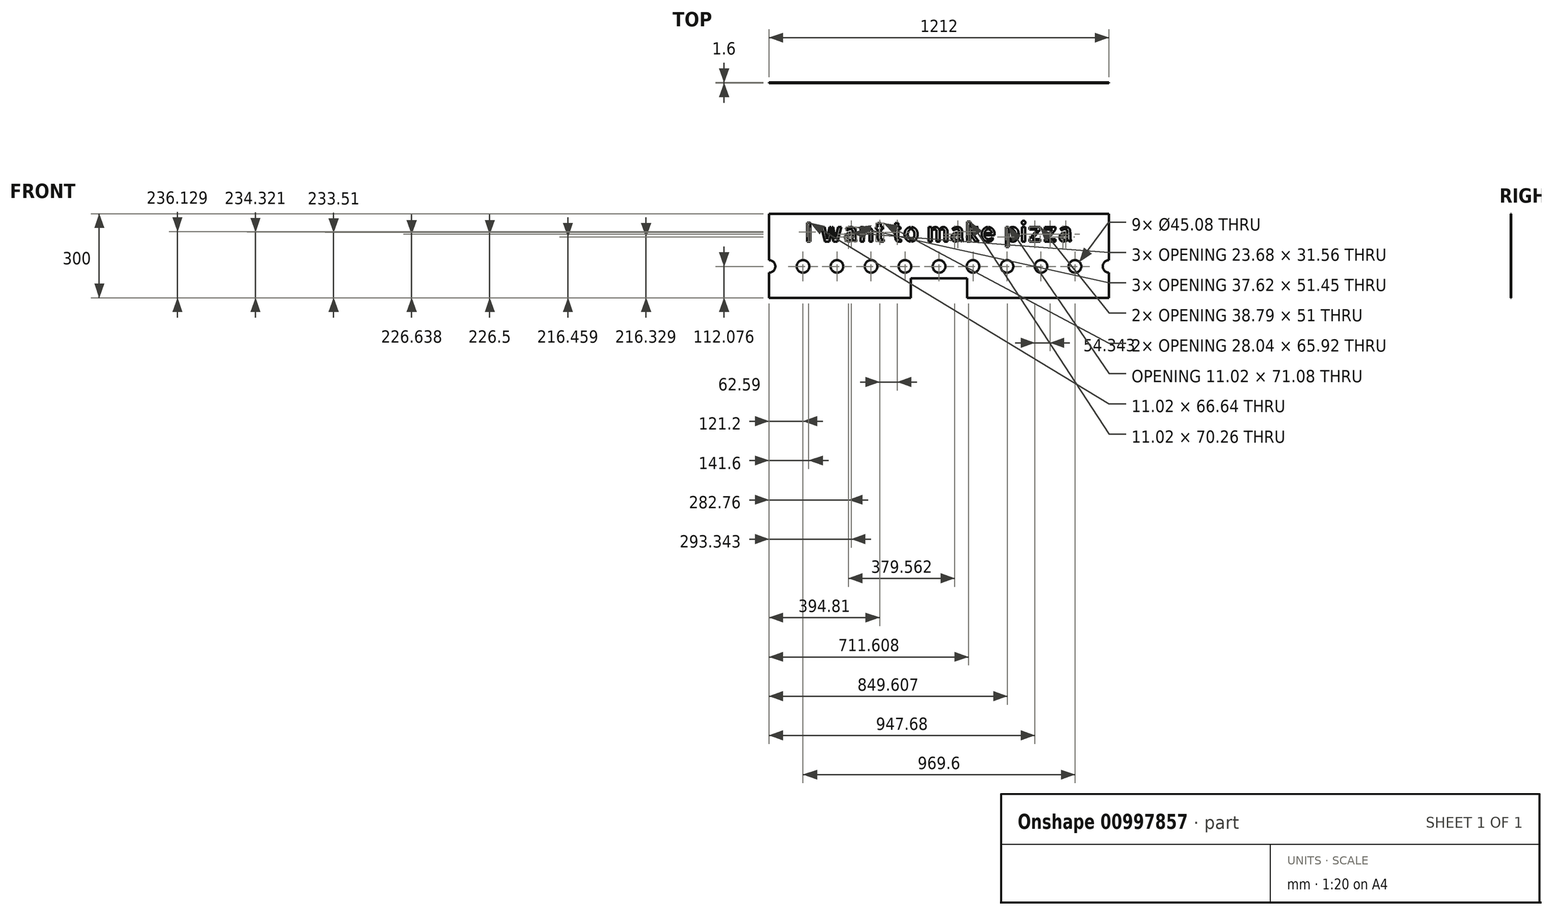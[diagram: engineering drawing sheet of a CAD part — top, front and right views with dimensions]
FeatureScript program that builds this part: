
annotation { "Feature Type Name" : "Feature", "Feature Type Description" : "" }
export const myFeature = defineFeature(function(context is Context, id is Id, definition is map)
    precondition{}
    {
        {
            var Q0;
            Q0=qCreatedBy(makeId("Front.planeOp"),FACE);
            var sketch = newSketch(context, id + "F0", { "sketchPlane" : qUnion([Q0])});
            skLineSegment(sketch, "E0.bottom", {"start": v(0, 0) * mm, "end": v(-506, 0) * mm});
            skLineSegment(sketch, "E0.top", {"start": v(0, 300) * mm, "end": v(-1212, 300) * mm});
            skLineSegment(sketch, "E0.left", {"start": v(0, 0) * mm, "end": v(0, 89.54) * mm});
            skLineSegment(sketch, "E0.right", {"start": v(-1212, 0) * mm, "end": v(-1212, 89.54) * mm});
            skLineSegment(sketch, "E1", {"start": v(-506, 0) * mm, "end": v(-506, 70) * mm});
            skLineSegment(sketch, "E2", {"start": v(-506, 70) * mm, "end": v(-706, 70) * mm});
            skLineSegment(sketch, "E3", {"start": v(-706, 70) * mm, "end": v(-706, 0) * mm});
            skPoint(sketch, "E4.orphan", {"position": v(-606, 0) * mm});
            skLineSegment(sketch, "E5.trimOffspring", {"start": v(-706, 0) * mm, "end": v(-1212, 0) * mm});
            skArc(sketch, "E6", {"start": v(-1212, 89.54) * mm, "mid": v(-1189.46, 112.08) * mm, "end": v(-1212, 134.62) * mm});
            skCircle(sketch, "E7.1.0.0", {"center": v(-1090.8, 112.08) * mm, "radius": 22.54 * mm});
            skCircle(sketch, "E7.2.0.0", {"center": v(-969.6, 112.08) * mm, "radius": 22.54 * mm});
            skCircle(sketch, "E7.3.0.0", {"center": v(-848.4, 112.08) * mm, "radius": 22.54 * mm});
            skCircle(sketch, "E7.4.0.0", {"center": v(-727.2, 112.08) * mm, "radius": 22.54 * mm});
            skCircle(sketch, "E7.5.0.0", {"center": v(-606, 112.08) * mm, "radius": 22.54 * mm});
            skCircle(sketch, "E7.6.0.0", {"center": v(-484.8, 112.08) * mm, "radius": 22.54 * mm});
            skCircle(sketch, "E7.7.0.0", {"center": v(-363.6, 112.08) * mm, "radius": 22.54 * mm});
            skCircle(sketch, "E7.8.0.0", {"center": v(-242.4, 112.08) * mm, "radius": 22.54 * mm});
            skCircle(sketch, "E7.9.0.0", {"center": v(-121.2, 112.08) * mm, "radius": 22.54 * mm});
            skArc(sketch, "E7.10.0.0", {"start": v(0, 134.62) * mm, "mid": v(-22.54, 112.08) * mm, "end": v(0, 89.54) * mm});
            skLineSegment(sketch, "E7.direction1", {"start": v(-1212, 112.08) * mm, "end": v(-1090.8, 112.08) * mm, "construction": true});
            skLineSegment(sketch, "E8.trimOffspring", {"start": v(0, 134.62) * mm, "end": v(0, 300) * mm});
            skLineSegment(sketch, "E9.trimOffspring", {"start": v(-1212, 134.62) * mm, "end": v(-1212, 300) * mm});
            skSolve(sketch);
        }
        {
            var Q0;
            Q0=makeQuery(id+"F0.imprint","IMPRINT",FACE,{"disambiguationData":[TD([[makeQuery(id+"F0.imprint","IMPRINT",EDGE,{"derivedFrom":sQuery(id+"F0.wireOp",EDGE,"E0.top")}),1.0]])]});
            var sketch = newSketch(context, id + "F1", { "sketchPlane" : qUnion([Q0])});
            skText(sketch, "E10", { "text": "I want to make pizza", "fontName": "AllertaStencil-Regular.ttf"});
            const initialGuessF1  = {"E10": [-1.08442, 0.201, 1, 0, 0.06667]};
            skSetInitialGuess(sketch, initialGuessF1);
            skSolve(sketch);
        }
        {
            var Q0;
            Q0=makeQuery(id+"F0.imprint","IMPRINT",FACE,{"disambiguationData":[TD([[makeQuery(id+"F0.imprint","IMPRINT",EDGE,{"derivedFrom":sQuery(id+"F0.wireOp",EDGE,"E0.top")}),1.0]])]});
            extrude(context, id + "F2", {"entities" : qUnion([Q0]), "depth" : 1.6 * mm, "offsetDistance" : 25 * mm});
        }
        {
            var Q0;
            Q0=makeQuery(id+"F1.imprint","IMPRINT",FACE,{"disambiguationData":[TD([[makeQuery(id+"F1.imprint","IMPRINT",EDGE,{"derivedFrom":sQuery(id+"F1.wireOp",EDGE,"E10.sketch_text.stroke-0")}),-1.0]])]});
            var Q1;
            Q1=makeQuery(id+"F1.imprint","IMPRINT",FACE,{"disambiguationData":[TD([[makeQuery(id+"F1.imprint","IMPRINT",EDGE,{"derivedFrom":sQuery(id+"F1.wireOp",EDGE,"E10.sketch_text.stroke-12")}),-1.0]])]});
            var Q2;
            Q2=makeQuery(id+"F1.imprint","IMPRINT",FACE,{"disambiguationData":[TD([[makeQuery(id+"F1.imprint","IMPRINT",EDGE,{"derivedFrom":sQuery(id+"F1.wireOp",EDGE,"E10.sketch_text.stroke-4")}),-1.0]])]});
            var Q3;
            Q3=makeQuery(id+"F1.imprint","IMPRINT",FACE,{"disambiguationData":[TD([[makeQuery(id+"F1.imprint","IMPRINT",EDGE,{"derivedFrom":sQuery(id+"F1.wireOp",EDGE,"E10.sketch_text.stroke-39")}),-1.0]])]});
            var Q4;
            Q4=makeQuery(id+"F1.imprint","IMPRINT",FACE,{"disambiguationData":[TD([[makeQuery(id+"F1.imprint","IMPRINT",EDGE,{"derivedFrom":sQuery(id+"F1.wireOp",EDGE,"E10.sketch_text.stroke-20")}),-1.0]])]});
            var Q5;
            Q5=makeQuery(id+"F1.imprint","IMPRINT",FACE,{"disambiguationData":[TD([[makeQuery(id+"F1.imprint","IMPRINT",EDGE,{"derivedFrom":sQuery(id+"F1.wireOp",EDGE,"E10.sketch_text.stroke-75")}),-1.0]])]});
            var Q6;
            Q6=makeQuery(id+"F1.imprint","IMPRINT",FACE,{"disambiguationData":[TD([[makeQuery(id+"F1.imprint","IMPRINT",EDGE,{"derivedFrom":sQuery(id+"F1.wireOp",EDGE,"E10.sketch_text.stroke-80")}),-1.0]])]});
            var Q7;
            Q7=makeQuery(id+"F1.imprint","IMPRINT",FACE,{"disambiguationData":[TD([[makeQuery(id+"F1.imprint","IMPRINT",EDGE,{"derivedFrom":sQuery(id+"F1.wireOp",EDGE,"E10.sketch_text.stroke-99")}),-1.0]])]});
            var Q8;
            Q8=makeQuery(id+"F1.imprint","IMPRINT",FACE,{"disambiguationData":[TD([[makeQuery(id+"F1.imprint","IMPRINT",EDGE,{"derivedFrom":sQuery(id+"F1.wireOp",EDGE,"E10.sketch_text.stroke-124")}),-1.0]])]});
            var Q9;
            Q9=makeQuery(id+"F1.imprint","IMPRINT",FACE,{"disambiguationData":[TD([[makeQuery(id+"F1.imprint","IMPRINT",EDGE,{"derivedFrom":sQuery(id+"F1.wireOp",EDGE,"E10.sketch_text.stroke-165")}),-1.0]])]});
            var Q10;
            Q10=makeQuery(id+"F1.imprint","IMPRINT",FACE,{"disambiguationData":[TD([[makeQuery(id+"F1.imprint","IMPRINT",EDGE,{"derivedFrom":sQuery(id+"F1.wireOp",EDGE,"E10.sketch_text.stroke-149")}),-1.0]])]});
            var Q11;
            Q11=makeQuery(id+"F1.imprint","IMPRINT",FACE,{"disambiguationData":[TD([[makeQuery(id+"F1.imprint","IMPRINT",EDGE,{"derivedFrom":sQuery(id+"F1.wireOp",EDGE,"E10.sketch_text.stroke-181")}),-1.0]])]});
            var Q12;
            Q12=makeQuery(id+"F1.imprint","IMPRINT",FACE,{"disambiguationData":[TD([[makeQuery(id+"F1.imprint","IMPRINT",EDGE,{"derivedFrom":sQuery(id+"F1.wireOp",EDGE,"E10.sketch_text.stroke-202")}),-1.0]])]});
            var Q13;
            Q13=makeQuery(id+"F1.imprint","IMPRINT",FACE,{"disambiguationData":[TD([[makeQuery(id+"F1.imprint","IMPRINT",EDGE,{"derivedFrom":sQuery(id+"F1.wireOp",EDGE,"E10.sketch_text.stroke-186")}),-1.0]])]});
            var Q14;
            Q14=makeQuery(id+"F1.imprint","IMPRINT",FACE,{"disambiguationData":[TD([[makeQuery(id+"F1.imprint","IMPRINT",EDGE,{"derivedFrom":sQuery(id+"F1.wireOp",EDGE,"E10.sketch_text.stroke-239")}),-1.0]])]});
            var Q15;
            Q15=makeQuery(id+"F1.imprint","IMPRINT",FACE,{"disambiguationData":[TD([[makeQuery(id+"F1.imprint","IMPRINT",EDGE,{"derivedFrom":sQuery(id+"F1.wireOp",EDGE,"E10.sketch_text.stroke-282")}),-1.0]])]});
            var Q16;
            Q16=makeQuery(id+"F1.imprint","IMPRINT",FACE,{"disambiguationData":[TD([[makeQuery(id+"F1.imprint","IMPRINT",EDGE,{"derivedFrom":sQuery(id+"F1.wireOp",EDGE,"E10.sketch_text.stroke-275")}),-1.0]])]});
            var Q17;
            Q17=makeQuery(id+"F1.imprint","IMPRINT",FACE,{"disambiguationData":[TD([[makeQuery(id+"F1.imprint","IMPRINT",EDGE,{"derivedFrom":sQuery(id+"F1.wireOp",EDGE,"E10.sketch_text.stroke-220")}),-1.0]])]});
            var Q18;
            Q18=makeQuery(id+"F1.imprint","IMPRINT",FACE,{"disambiguationData":[TD([[makeQuery(id+"F1.imprint","IMPRINT",EDGE,{"derivedFrom":sQuery(id+"F1.wireOp",EDGE,"E10.sketch_text.stroke-299")}),-1.0]])]});
            extrude(context, id + "F3", {"entities" : qUnion([Q0, Q1, Q2, Q3, Q4, Q5, Q6, Q7, Q8, Q9, Q10, Q11, Q12, Q13, Q14, Q15, Q16, Q17, Q18]), "operationType" : NewBodyOperationType.REMOVE, "depth" : 25 * mm, "offsetDistance" : 25 * mm});
        }
        {
            var Q0;
            Q0=makeQuery(id+"F1.imprint","IMPRINT",FACE,{"disambiguationData":[TD([[makeQuery(id+"F1.imprint","IMPRINT",EDGE,{"derivedFrom":sQuery(id+"F1.wireOp",EDGE,"E10.sketch_text.stroke-286")}),-1.0]])]});
            var Q1;
            Q1=makeQuery(id+"F1.imprint","IMPRINT",FACE,{"disambiguationData":[TD([[makeQuery(id+"F1.imprint","IMPRINT",EDGE,{"derivedFrom":sQuery(id+"F1.wireOp",EDGE,"E10.sketch_text.stroke-323")}),-1.0]])]});
            var Q2;
            Q2=makeQuery(id+"F1.imprint","IMPRINT",FACE,{"disambiguationData":[TD([[makeQuery(id+"F1.imprint","IMPRINT",EDGE,{"derivedFrom":sQuery(id+"F1.wireOp",EDGE,"E10.sketch_text.stroke-328")}),-1.0]])]});
            var Q3;
            Q3=makeQuery(id+"F1.imprint","IMPRINT",FACE,{"disambiguationData":[TD([[makeQuery(id+"F1.imprint","IMPRINT",EDGE,{"derivedFrom":sQuery(id+"F1.wireOp",EDGE,"E10.sketch_text.stroke-358")}),-1.0]])]});
            var Q4;
            Q4=makeQuery(id+"F1.imprint","IMPRINT",FACE,{"disambiguationData":[TD([[makeQuery(id+"F1.imprint","IMPRINT",EDGE,{"derivedFrom":sQuery(id+"F1.wireOp",EDGE,"E10.sketch_text.stroke-354")}),-1.0]])]});
            var Q5;
            Q5=makeQuery(id+"F1.imprint","IMPRINT",FACE,{"disambiguationData":[TD([[makeQuery(id+"F1.imprint","IMPRINT",EDGE,{"derivedFrom":sQuery(id+"F1.wireOp",EDGE,"E10.sketch_text.stroke-366")}),-1.0]])]});
            var Q6;
            Q6=makeQuery(id+"F1.imprint","IMPRINT",FACE,{"disambiguationData":[TD([[makeQuery(id+"F1.imprint","IMPRINT",EDGE,{"derivedFrom":sQuery(id+"F1.wireOp",EDGE,"E10.sketch_text.stroke-378")}),-1.0]])]});
            var Q7;
            Q7=makeQuery(id+"F1.imprint","IMPRINT",FACE,{"disambiguationData":[TD([[makeQuery(id+"F1.imprint","IMPRINT",EDGE,{"derivedFrom":sQuery(id+"F1.wireOp",EDGE,"E10.sketch_text.stroke-409")}),-1.0]])]});
            var Q8;
            Q8=makeQuery(id+"F1.imprint","IMPRINT",FACE,{"disambiguationData":[TD([[makeQuery(id+"F1.imprint","IMPRINT",EDGE,{"derivedFrom":sQuery(id+"F1.wireOp",EDGE,"E10.sketch_text.stroke-390")}),-1.0]])]});
            extrude(context, id + "F4", {"entities" : qUnion([Q0, Q1, Q2, Q3, Q4, Q5, Q6, Q7, Q8]), "operationType" : NewBodyOperationType.REMOVE, "depth" : 25 * mm, "offsetDistance" : 25 * mm});
        }
    });
